# Revit family: PRD_AR_PprTwlDpnsrs_STRATOSCombinationPaperTowelAndSoapDispenser_STR600_STR601
name_source: partatom
category: Specialty Equipment
units: mm (PartAtom-declared; Revit-internal decimal feet)

## family parameters
Cut with Voids When Loaded = No
Host = Face
OmniClass Number = 23.40.20.21
OmniClass Title = Toilet and Bath Specialties
Part Type = Normal
Room Calculation Point = No
Round Connector Dimension = Use Diameter
Shared = No

## types (2) — shared parameters
AssetType = Fixed
Color = Stainless steel
Default Elevation = 1200 mm
DispenserMaterial = PRD_AR_StainlessSteel_SatinFinished
DurationUnit = year
Features = For wall mounting. Stainless steel, surface satin finished.
FillingQuantity1 = 400 towels
Finish = Satin finished
Form = Wall mounted
IfcExportAs = IfcFurnitureType
IfcExportType = NOTDEFINED
IntegralAccessories = Incl. stainless steel screws and dowels
Lock = key-lock
MainColor = Stainless steel
Manufacturer = KWC Group Management AG
ManufacturerName = KWC Group Management AG
ManufacturerURL = www.kwc-professional.com
Material = Stainless steel
MaterialCode = Stainless steel 1.4301
NominalDepth = 134 mm
Operation = Manual
ProductInformation = http://pim.kwc.com
Style = Paper towel dispenser
TypeOfConsumable1 = Paper towel
TypeOfFixing = Screw
TypeOfMounting = Wall mounting
TypeOfOperation = Manual operation
URL = www.kwc-professional.com
Uniclass2015Version = Products v1.10
Version = 1
WarrantyDurationUnit = year

## per-type parameters (varying)
| type | BIMObjectName | Category | Description | FillingQuantity2 | GrossWeight | ModelNumber | NBSDescription | NBSReference | Name | NetWeight | NominalHeight | NominalLength | NominalWidth | STR600 | STR601 | Size | TypeOfConsumable2 | Uniclass2015Code | Uniclass2015Title |
| STR601 | PRD_AR_DispensersAndAcceptanceUnits_STRATOSCombinationPaperTowelAndSoapDispenser_STR601 | Pr_40_70_22, Dispensers and acceptance units | STRATOS paper towel and soap dispenser combination for wall mounting, stainless steel, surface satin finished, material thickness 1.5 mm, curved front with two viewing windows, cylinder lock with key, paper towel dispenser capacity 300-400 pieces for paper with Z-fold, soap dispenser suitable for liquid soap or lotion, 800 ml refill container, with plastic push lever, including mounting material. | 0.8 liter | 5.00 kg | 3600008934 | Dispensers and acceptance units |  | STRATOS Combination Paper Towel And Soap Dispenser STR601 | 4.67 kg | 304 mm  [stored 0.997375 ft] | 396 mm  [stored 1.29921 ft] | 396 mm  [stored 1.29921 ft] | No | Yes | 396 x 304 x 134 mm | Liquid soap | Pr_40_70_22 |  |
| STR600 | PRD_AR_PaperTowelDispensers_STRATOSPaperTowelDispenser_STR600 | Pr_40_70_22_62, Paper towel dispensers | STRATOS paper towel dispenser for wall mounting, stainless steel, surface satin finished, material thickness 1.5 mm, curved front with inspection window, cylinder lock with key, capacity 300-400 pieces for paper with Z-fold, including mounting material. |  | 3.86 kg | 3600008935 | Paper towel dispensers | 45-35-72/344 | STRATOS paper towel dispenser STR600 | 3.40 kg | 305 mm  [stored 1.00066 ft] | 300 mm  [stored 0.984252 ft] | 300 mm  [stored 0.984252 ft] | Yes | No | 300 x 305 x 134 mm |  | Pr_40_70_22_62 | Paper towel dispensers |

note: column(s) folded — value = type name in every type: Model, ModelReference

note: [stored X ft] marks values corroborated as IEEE doubles in the binary element streams (Revit-internal decimal feet)

## geometry (parser evidence)
native form markers: Sweep x2
no freeform markers — native parametric forms only
